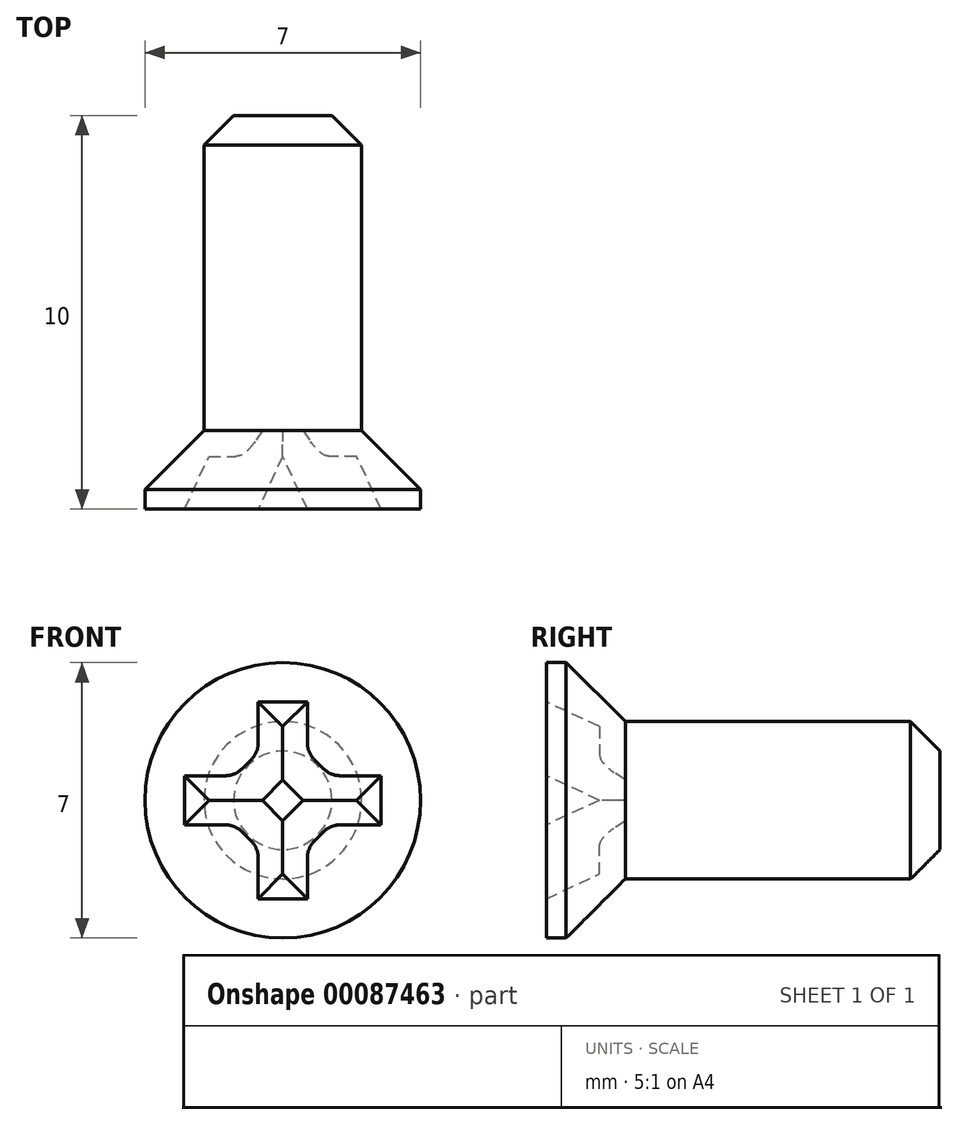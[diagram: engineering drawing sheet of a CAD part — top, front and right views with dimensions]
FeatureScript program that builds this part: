
annotation { "Feature Type Name" : "Feature", "Feature Type Description" : "" }
export const myFeature = defineFeature(function(context is Context, id is Id, definition is map)
    precondition{}
    {
        {
            var Q0;
            Q0=qCreatedBy(makeId("Right.planeOp"),FACE);
            var sketch = newSketch(context, id + "F0", { "sketchPlane" : qUnion([Q0])});
            skLineSegment(sketch, "E0", {"start": v(-4.9, 0) * mm, "end": v(9.48, 0) * mm, "construction": true});
            skLineSegment(sketch, "E1", {"start": v(8, 0) * mm, "end": v(8, 2) * mm});
            skLineSegment(sketch, "E2", {"start": v(8, 2) * mm, "end": v(0, 2) * mm});
            skLineSegment(sketch, "E3", {"start": v(0, 2) * mm, "end": v(-1.5, 3.5) * mm});
            skLineSegment(sketch, "E4", {"start": v(-1.5, 3.5) * mm, "end": v(-2, 3.5) * mm});
            skLineSegment(sketch, "E5", {"start": v(-2, 3.5) * mm, "end": v(-2, 0) * mm});
            skLineSegment(sketch, "E6", {"start": v(-2, 0) * mm, "end": v(8, 0) * mm});
            skSolve(sketch);
        }
        {
            var Q0;
            Q0=qSketchRegion(id+"F0",true);
            var Q1;
            Q1=sQuery(id+"F0.wireOp",EDGE,"E0");
            revolve(context, id + "F1", {"entities" : qUnion([Q0]), "axis" : qUnion([Q1]), "revolveType" : RevolveType.FULL});
        }
        {
            var Q0;
            Q0=makeQuery(id+"F1.opRevolve","SWEPT_EDGE",EDGE,{"disambiguationData":[OSD([sQuery(id+"F0.wireOp",EDGE,"E1"),sQuery(id+"F0.wireOp",EDGE,"E2")])]});
            chamfer(context, id + "F2", {"entities" : qUnion([Q0]), "width" : 0.75 * mm, "tangentPropagation" : true});
        }
        {
            var Q0;
            Q0=makeQuery(id+"F1.opRevolve","SWEPT_FACE",FACE,{"disambiguationData":[OSD([sQuery(id+"F0.wireOp",EDGE,"E5")])]});
            var sketch = newSketch(context, id + "F3", { "sketchPlane" : qUnion([Q0])});
            skLineSegment(sketch, "E7.bottom", {"start": v(0.62, 2.5) * mm, "end": v(-0.63, 2.5) * mm});
            skLineSegment(sketch, "E7.top", {"start": v(0.63, -2.5) * mm, "end": v(-0.63, -2.5) * mm});
            skLineSegment(sketch, "E7.left", {"start": v(0.62, 2.5) * mm, "end": v(0.63, -2.5) * mm});
            skLineSegment(sketch, "E7.right", {"start": v(-0.63, 2.5) * mm, "end": v(-0.63, -2.5) * mm});
            skPoint(sketch, "E7.middle", {"position": v(0, 0) * mm});
            skLineSegment(sketch, "E8.bottom", {"start": v(2.5, -0.62) * mm, "end": v(-2.5, -0.62) * mm});
            skLineSegment(sketch, "E8.top", {"start": v(2.5, 0.63) * mm, "end": v(-2.5, 0.62) * mm});
            skLineSegment(sketch, "E8.left", {"start": v(2.5, -0.62) * mm, "end": v(2.5, 0.63) * mm});
            skLineSegment(sketch, "E8.right", {"start": v(-2.5, -0.63) * mm, "end": v(-2.5, 0.62) * mm});
            skLineSegment(sketch, "E9.bottom", {"start": v(1.84, 0) * mm, "end": v(0, 1.84) * mm});
            skLineSegment(sketch, "E9.top", {"start": v(0, -1.84) * mm, "end": v(-1.84, 0) * mm});
            skLineSegment(sketch, "E9.left", {"start": v(1.84, 0) * mm, "end": v(0, -1.84) * mm});
            skLineSegment(sketch, "E9.right", {"start": v(0, 1.84) * mm, "end": v(-1.84, 0) * mm});
            skSolve(sketch);
        }
        {
            var Q0;
            Q0=makeQuery(id+"F1.opRevolve","SWEPT_FACE",FACE,{"disambiguationData":[OSD([sQuery(id+"F0.wireOp",EDGE,"E5")])]});
            var sketch = newSketch(context, id + "F4", { "sketchPlane" : qUnion([Q0])});
            skLineSegment(sketch, "E10.0", {"start": v(0.62, 2.5) * mm, "end": v(-0.63, 2.5) * mm});
            skLineSegment(sketch, "E10.1", {"start": v(0.63, -2.5) * mm, "end": v(-0.63, -2.5) * mm});
            skLineSegment(sketch, "E10.2", {"start": v(0.62, 2.5) * mm, "end": v(0.62, 1.21) * mm});
            skLineSegment(sketch, "E10.3", {"start": v(-0.63, 2.5) * mm, "end": v(-0.63, 1.21) * mm});
            skLineSegment(sketch, "E10.5", {"start": v(2.5, -0.62) * mm, "end": v(1.21, -0.62) * mm});
            skLineSegment(sketch, "E10.6", {"start": v(2.5, 0.63) * mm, "end": v(1.21, 0.63) * mm});
            skLineSegment(sketch, "E10.7", {"start": v(2.5, -0.62) * mm, "end": v(2.5, 0.63) * mm});
            skLineSegment(sketch, "E10.8", {"start": v(-2.5, -0.63) * mm, "end": v(-2.5, 0.62) * mm});
            skLineSegment(sketch, "E10.10", {"start": v(1.21, 0.63) * mm, "end": v(0.62, 1.21) * mm});
            skLineSegment(sketch, "E10.11", {"start": v(-0.63, -1.21) * mm, "end": v(-1.21, -0.63) * mm});
            skLineSegment(sketch, "E10.12", {"start": v(1.21, -0.62) * mm, "end": v(0.63, -1.21) * mm});
            skLineSegment(sketch, "E10.13", {"start": v(-0.63, 1.21) * mm, "end": v(-1.21, 0.62) * mm});
            skLineSegment(sketch, "E11.trimOffspring", {"start": v(-1.21, 0.62) * mm, "end": v(-2.5, 0.62) * mm});
            skLineSegment(sketch, "E12.trimOffspring", {"start": v(-0.63, -1.21) * mm, "end": v(-0.63, -2.5) * mm});
            skLineSegment(sketch, "E13.trimOffspring", {"start": v(-1.21, -0.62) * mm, "end": v(-2.5, -0.62) * mm});
            skLineSegment(sketch, "E14.trimOffspring", {"start": v(0.63, -1.21) * mm, "end": v(0.63, -2.5) * mm});
            skSolve(sketch);
        }
        {
            var Q0;
            Q0=qSketchRegion(id+"F4",true);
            extrude(context, id + "F5", {"entities" : qUnion([Q0]), "operationType" : NewBodyOperationType.REMOVE, "oppositeDirection" : true, "depth" : 2 * mm, "hasDraft" : true, "draftAngle" : 25 * degree, "draftPullDirection" : true});
        }
        {
            var Q0;
            Q0=makeQuery(id+"F5.boolean.opBoolean","COPY",EDGE,{"derivedFrom":makeQuery(id+"F5.opExtrude","SWEPT_EDGE",EDGE,{"disambiguationData":[OSD([sQuery(id+"F4.wireOp",EDGE,"E10.3"),sQuery(id+"F4.wireOp",EDGE,"E10.13")])]})});
            var Q1;
            Q1=makeQuery(id+"F5.boolean.opBoolean","COPY",EDGE,{"derivedFrom":makeQuery(id+"F5.opExtrude","SWEPT_EDGE",EDGE,{"disambiguationData":[OSD([sQuery(id+"F4.wireOp",EDGE,"E10.13"),sQuery(id+"F4.wireOp",EDGE,"E11.trimOffspring")])]})});
            var Q2;
            Q2=makeQuery(id+"F5.boolean.opBoolean","COPY",EDGE,{"derivedFrom":makeQuery(id+"F5.opExtrude","SWEPT_EDGE",EDGE,{"disambiguationData":[OSD([sQuery(id+"F4.wireOp",EDGE,"E10.2"),sQuery(id+"F4.wireOp",EDGE,"E10.10")])]})});
            var Q3;
            Q3=makeQuery(id+"F5.boolean.opBoolean","COPY",EDGE,{"derivedFrom":makeQuery(id+"F5.opExtrude","SWEPT_EDGE",EDGE,{"disambiguationData":[OSD([sQuery(id+"F4.wireOp",EDGE,"E10.6"),sQuery(id+"F4.wireOp",EDGE,"E10.10")])]})});
            var Q4;
            Q4=makeQuery(id+"F5.boolean.opBoolean","COPY",EDGE,{"derivedFrom":makeQuery(id+"F5.opExtrude","SWEPT_EDGE",EDGE,{"disambiguationData":[OSD([sQuery(id+"F4.wireOp",EDGE,"E10.5"),sQuery(id+"F4.wireOp",EDGE,"E10.12")])]})});
            var Q5;
            Q5=makeQuery(id+"F5.boolean.opBoolean","COPY",EDGE,{"derivedFrom":makeQuery(id+"F5.opExtrude","SWEPT_EDGE",EDGE,{"disambiguationData":[OSD([sQuery(id+"F4.wireOp",EDGE,"E10.12"),sQuery(id+"F4.wireOp",EDGE,"E14.trimOffspring")])]})});
            var Q6;
            Q6=makeQuery(id+"F5.boolean.opBoolean","COPY",EDGE,{"derivedFrom":makeQuery(id+"F5.opExtrude","SWEPT_EDGE",EDGE,{"disambiguationData":[OSD([sQuery(id+"F4.wireOp",EDGE,"E10.11"),sQuery(id+"F4.wireOp",EDGE,"E13.trimOffspring")])]})});
            var Q7;
            Q7=makeQuery(id+"F5.boolean.opBoolean","COPY",EDGE,{"derivedFrom":makeQuery(id+"F5.opExtrude","SWEPT_EDGE",EDGE,{"disambiguationData":[OSD([sQuery(id+"F4.wireOp",EDGE,"E10.11"),sQuery(id+"F4.wireOp",EDGE,"E12.trimOffspring")])]})});
            fillet(context, id + "F6", {"entities" : qUnion([Q0, Q1, Q2, Q3, Q4, Q5, Q6, Q7]), "radius" : 0.65 * mm, "tangentPropagation" : true, "allowEdgeOverflow" : false});
        }
    });
